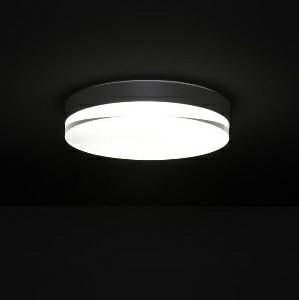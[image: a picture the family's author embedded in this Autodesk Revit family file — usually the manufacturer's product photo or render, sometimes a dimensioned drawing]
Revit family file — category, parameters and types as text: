
# Revit family: spectral_perga_perga-ra_420_4300-840_ws_b521
name_source: partatom
category: Lighting Fixtures
revit_build: Autodesk Revit 2016 (Build: 20150220_1215(x64)
units: mm (PartAtom-declared; Revit-internal decimal feet)

## family parameters
Cut with Voids When Loaded = No
Host = Face
Light Source = No
Part Type = Normal
Room Calculation Point = No
Round Connector Dimension = Use Diameter
Shared = No

## types (1)
- SPECTRAL PERGA (1 x )
    Apparent Load = 0 VA
    Approval mark = CE
    CIE Flux Codes = 46 78 95 88 63
    Control Gear = Electronic transformer
    Default Elevation = 1800 mm
    Description = SPP0000009
PERGAMENT surface mounted

Design:
Round luminaire element comprising an acrylic glass block with transparent superpolished exterior. Underneath painted matt to reduce glare. Luminaire
element integrated in an outer steel powder-coated sectional aluminium cylindrical frame. The acrylic block is scratchproof and insensitive to fingerprints, and is connected to a poweder-coated metal body by a bayonet and snap fastening.. The metal body accommodates the electrical components and electronic ballast. The LED module is formed as a round LED flat board and can be removed for installation or exchange using a key-hole screw connection. Electrical connection of the flat LED board by means of a plug. Luminaire with heat-resistant wiring. Homogenous illumination of the light surface. Suitable for ceiling or wall mounting. Light colours 830 or 840. Also in a dimmable version. Protection rating IP20, safety class I.

Colour:
Metal body – similar to RAL 9016 white silk matt
Frame – white (WS), silver (SI), black (AQ)
    Height = 98 mm
    Lamp = 1 x
    Lamp count = 1
    Length = 422 mm
    Luminous efficacy = 0 lm/W
    Manufacturer = Ridi
    ModVariant = No
    Model = PERGA-RA 420/4300-840 WS
    Mounting Place = Ceiling
    Mounting Type = Surface mounted
    Number of Poles = 1
    OnlyDefault = Yes
    Power Factor = 1
    Product Name = SPECTRAL PERGA
    Product group = Ceiling mounted luminaire
    ProductGroupID = 3
    Protection Class = Protection class
    Protection Degree = IP 20
    RlxData = <blob elided: 29773 chars, md5=acad3a1b>
    Socket = socket
    Standby Power = 0 W
    System Light Flux = 0 lm
    System Power = 0 W
    Type Image = pergamentdgr03.jpg
    URL = http://reluxnet.relux.com
    VarID = 1
    Voltage = 0 V
    Weight = 0.00 kg
    Width = 0 mm  [stored 0 ft]

note: [stored X ft] marks values corroborated as IEEE doubles in the binary element streams (Revit-internal decimal feet)

## geometry (parser evidence)
native form markers: Sweep x12
no freeform markers — native parametric forms only
